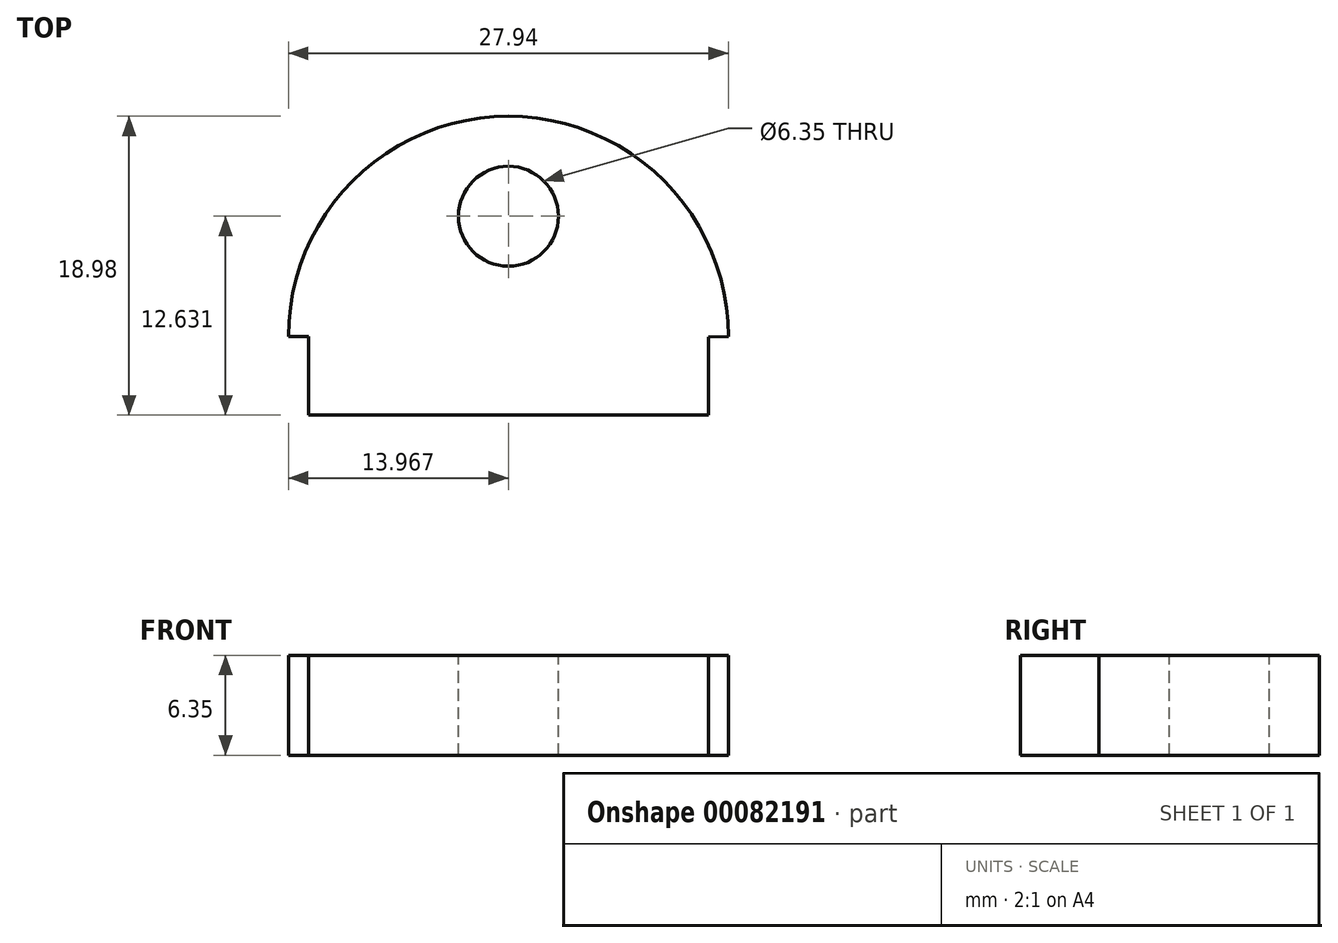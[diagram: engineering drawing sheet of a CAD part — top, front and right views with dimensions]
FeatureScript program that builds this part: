
annotation { "Feature Type Name" : "Feature", "Feature Type Description" : "" }
export const myFeature = defineFeature(function(context is Context, id is Id, definition is map)
    precondition{}
    {
        {
            var Q0;
            Q0=qCreatedBy(makeId("Top.planeOp"),FACE);
            var sketch = newSketch(context, id + "F0", { "sketchPlane" : qUnion([Q0])});
            skLineSegment(sketch, "E0", {"start": v(-20, -36.76) * mm, "end": v(-20, -31.76) * mm});
            skLineSegment(sketch, "E1", {"start": v(5.4, -31.78) * mm, "end": v(5.4, -36.76) * mm});
            skLineSegment(sketch, "E2", {"start": v(5.4, -36.76) * mm, "end": v(-20, -36.76) * mm});
            skArc(sketch, "E3", {"start": v(6.67, -31.76) * mm, "mid": v(-7.3, -17.78) * mm, "end": v(-21.27, -31.76) * mm});
            skLineSegment(sketch, "E4", {"start": v(-21.27, -31.76) * mm, "end": v(-20, -31.76) * mm});
            skPoint(sketch, "E5", {"position": v(-7.3, -36.76) * mm});
            skLineSegment(sketch, "E6", {"start": v(5.4, -31.78) * mm, "end": v(6.67, -31.76) * mm});
            skSolve(sketch);
        }
        {
            var Q0;
            Q0 = qSketchRegion(id + "F0", true);
            extrude(context, id + "F1", {"entities" : qUnion([Q0]), "depth" : 6.35 * mm});
        }
        {
            var Q0;
            Q0=makeQuery(id+"F1.opExtrude","CAP_FACE",FACE,{"disambiguationData":[OSD([sQuery(id+"F0.wireOp",EDGE,"E0"),sQuery(id+"F0.wireOp",EDGE,"E1"),sQuery(id+"F0.wireOp",EDGE,"E2"),sQuery(id+"F0.wireOp",EDGE,"E3"),sQuery(id+"F0.wireOp",EDGE,"E4")])],"isStart":false});
            var sketch = newSketch(context, id + "F2", { "sketchPlane" : qUnion([Q0])});
            skPoint(sketch, "E7", {"position": v(-7.3, -17.78) * mm});
            skPoint(sketch, "E8", {"position": v(-7.3, -24.13) * mm});
            skCircle(sketch, "E9", {"center": v(-7.3, -24.13) * mm, "radius": 3.17 * mm});
            skSolve(sketch);
        }
        {
            var Q0;
            Q0 = qSketchRegion(id + "F2", true);
            extrude(context, id + "F3", {"entities" : qUnion([Q0]), "operationType" : NewBodyOperationType.REMOVE, "oppositeDirection" : true, "depth" : 25.4 * mm});
        }
    });
